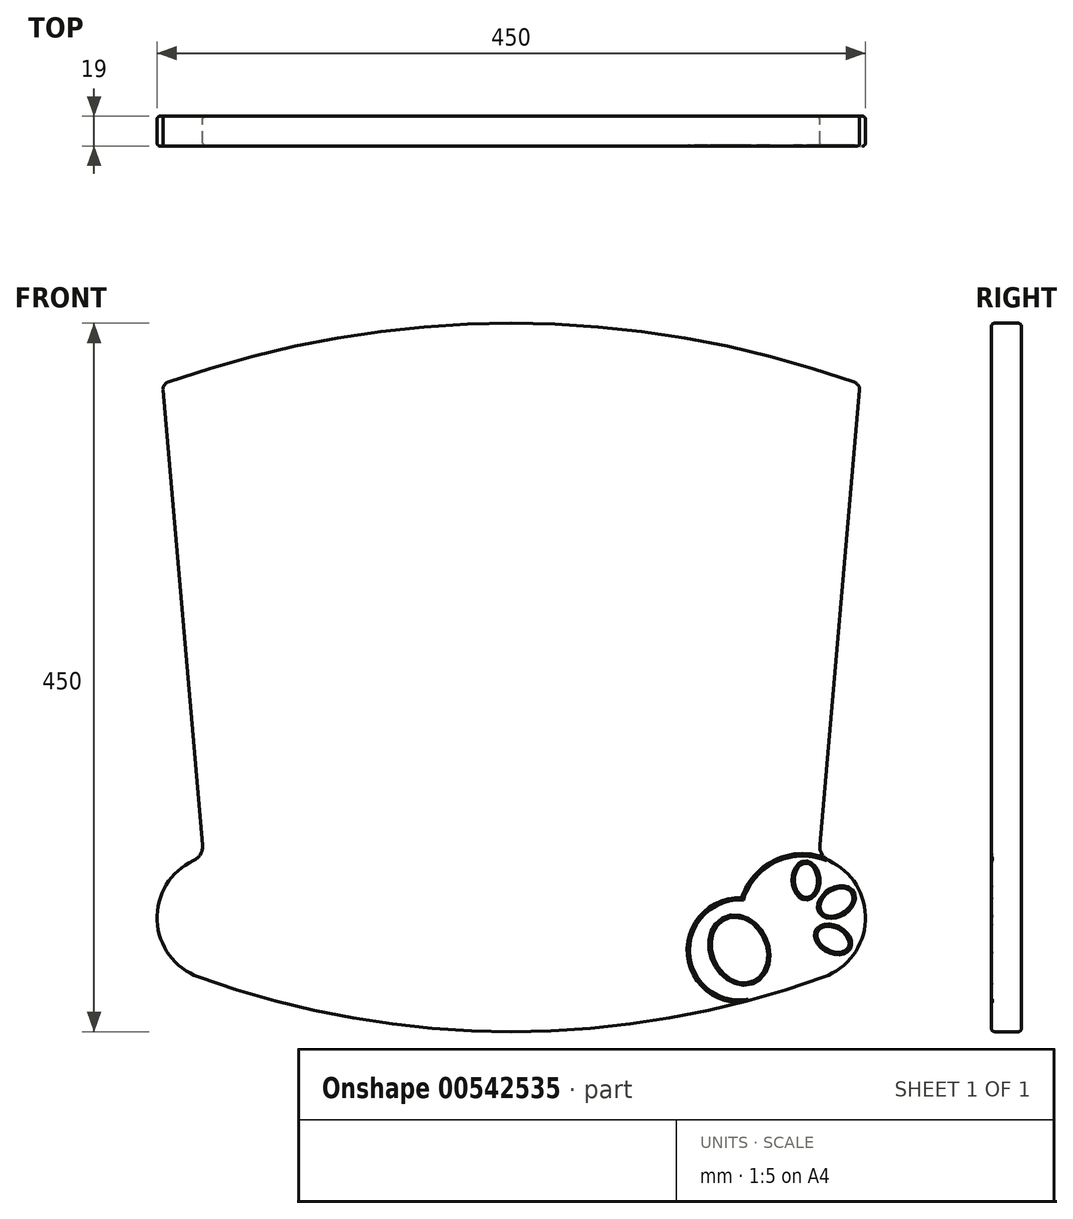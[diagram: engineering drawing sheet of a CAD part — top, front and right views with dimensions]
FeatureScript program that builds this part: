
annotation { "Feature Type Name" : "Feature", "Feature Type Description" : "" }
export const myFeature = defineFeature(function(context is Context, id is Id, definition is map)
    precondition{}
    {
        {
            var Q0;
            Q0=qCreatedBy(makeId("Front.planeOp"),FACE);
            var sketch = newSketch(context, id + "F0", { "sketchPlane" : qUnion([Q0])});
            skLineSegment(sketch, "E0.bottom", {"start": v(225, 450) * mm, "end": v(-225, 450) * mm, "construction": true});
            skLineSegment(sketch, "E0.top", {"start": v(225, 0) * mm, "end": v(-225, 0) * mm, "construction": true});
            skLineSegment(sketch, "E0.left", {"start": v(225, 450) * mm, "end": v(225, 0) * mm, "construction": true});
            skLineSegment(sketch, "E0.right", {"start": v(-225, 450) * mm, "end": v(-225, 0) * mm, "construction": true});
            skArc(sketch, "E1", {"start": v(-198.58, 34.73) * mm, "mid": v(-100.8, 8.75) * mm, "end": v(0, 0) * mm});
            skLineSegment(sketch, "E2", {"start": v(0, 449.93) * mm, "end": v(0, 0) * mm, "construction": true});
            skArc(sketch, "E3", {"start": v(-201.78, 108.67) * mm, "mid": v(-224.96, 70.63) * mm, "end": v(-198.58, 34.73) * mm});
            skPoint(sketch, "E4.orphan", {"position": v(-225, 45) * mm});
            skLineSegment(sketch, "E5", {"start": v(-221.27, 407.4) * mm, "end": v(-196, 118.62) * mm});
            skPoint(sketch, "E6.visualSharp", {"position": v(-195.34, 111) * mm});
            skArc(sketch, "E6.filletArc", {"start": v(-201.78, 108.67) * mm, "mid": v(-197.32, 112.73) * mm, "end": v(-196, 118.62) * mm});
            skArc(sketch, "E7", {"start": v(217.96, 412.54) * mm, "mid": v(0, 450) * mm, "end": v(-217.96, 412.54) * mm});
            skPoint(sketch, "E8.orphan", {"position": v(225, 45) * mm});
            skLineSegment(sketch, "E9.MirrorCS", {"start": v(221.27, 407.4) * mm, "end": v(196, 118.62) * mm});
            skArc(sketch, "E10.MirrorCS", {"start": v(198.58, 34.73) * mm, "mid": v(100.8, 8.75) * mm, "end": v(0, 0) * mm});
            skArc(sketch, "E11.MirrorCS", {"start": v(201.78, 108.67) * mm, "mid": v(224.96, 70.63) * mm, "end": v(198.58, 34.73) * mm});
            skArc(sketch, "E12.MirrorCS", {"start": v(201.78, 108.67) * mm, "mid": v(197.32, 112.73) * mm, "end": v(196, 118.62) * mm});
            skPoint(sketch, "E13.newPointA", {"position": v(-225, 450) * mm});
            skPoint(sketch, "E13.newPointB", {"position": v(-225, 410) * mm});
            skArc(sketch, "E13.filletArc", {"start": v(-217.96, 412.54) * mm, "mid": v(-220.5, 410.53) * mm, "end": v(-221.27, 407.4) * mm});
            skPoint(sketch, "E14.newPointA", {"position": v(225, 410) * mm});
            skPoint(sketch, "E14.newPointB", {"position": v(225, 450) * mm});
            skArc(sketch, "E14.filletArc", {"start": v(221.27, 407.4) * mm, "mid": v(220.5, 410.53) * mm, "end": v(217.96, 412.54) * mm});
            skSolve(sketch);
        }
        {
            var Q0;
            Q0=makeQuery(id+"F0.imprint","IMPRINT",FACE,{"disambiguationData":[TD([[makeQuery(id+"F0.imprint","IMPRINT",EDGE,{"derivedFrom":sQuery(id+"F0.wireOp",EDGE,"E1")}),1.0]])]});
            extrude(context, id + "F1", {"entities" : qUnion([Q0]), "depth" : 19 * mm, "offsetDistance" : 25 * mm});
        }
        {
            var Q0;
            Q0=makeQuery(id+"F1.opExtrude","CAP_FACE",FACE,{"disambiguationData":[OSD([sQuery(id+"F0.wireOp",EDGE,"E1"),sQuery(id+"F0.wireOp",EDGE,"E3"),sQuery(id+"F0.wireOp",EDGE,"E5"),sQuery(id+"F0.wireOp",EDGE,"E6.filletArc"),sQuery(id+"F0.wireOp",EDGE,"E7"),sQuery(id+"F0.wireOp",EDGE,"E9.MirrorCS"),sQuery(id+"F0.wireOp",EDGE,"E10.MirrorCS"),sQuery(id+"F0.wireOp",EDGE,"E11.MirrorCS"),sQuery(id+"F0.wireOp",EDGE,"E12.MirrorCS"),sQuery(id+"F0.wireOp",EDGE,"E13.filletArc"),sQuery(id+"F0.wireOp",EDGE,"E14.filletArc")])],"isStart":false});
            var sketch = newSketch(context, id + "F2", { "sketchPlane" : qUnion([Q0])});
            skArc(sketch, "E15", {"start": v(-153.47, 20.49) * mm, "mid": v(-112.62, 48.48) * mm, "end": v(-146.82, 84.3) * mm});
            skArc(sketch, "E16", {"start": v(146.82, 84.3) * mm, "mid": v(112.62, 48.48) * mm, "end": v(153.47, 20.49) * mm});
            skArc(sketch, "E17", {"start": v(201.78, 108.67) * mm, "mid": v(168.78, 108.92) * mm, "end": v(146.82, 84.3) * mm});
            skArc(sketch, "E18", {"start": v(-146.82, 84.3) * mm, "mid": v(-168.78, 108.92) * mm, "end": v(-201.78, 108.67) * mm});
            skEllipse(sketch, "E19", {"center": v(-187.19, 96) * mm, "majorRadius": 11.57 * mm, "minorRadius": 8.01 * mm, "majorAxis": v(-0.04, -1)});
            skEllipse(sketch, "E20.1.0", {"center": v(-206.57, 82.29) * mm, "majorRadius": 11.57 * mm, "minorRadius": 8.01 * mm, "majorAxis": v(0.84, -0.53)});
            skEllipse(sketch, "E20.2.0", {"center": v(-204.38, 58.65) * mm, "majorRadius": 11.57 * mm, "minorRadius": 8.01 * mm, "majorAxis": v(0.89, 0.46)});
            skLineSegment(sketch, "E20.anchor1", {"start": v(-185, 72.36) * mm, "end": v(-187.19, 96) * mm, "construction": true});
            skLineSegment(sketch, "E20.anchor2", {"start": v(-185, 72.36) * mm, "end": v(-204.38, 58.65) * mm, "construction": true});
            skLineSegment(sketch, "E21", {"start": v(0, 0) * mm, "end": v(0, 96.92) * mm, "construction": true});
            skLineSegment(sketch, "E22", {"start": v(0, 96.92) * mm, "end": v(0, 74.03) * mm});
            skEllipse(sketch, "E23", {"center": v(-144.94, 51.85) * mm, "majorRadius": 17.47 * mm, "minorRadius": 21.85 * mm, "majorAxis": v(-0.92, 0.4)});
            skEllipse(sketch, "E24.MirrorC", {"center": v(144.94, 51.85) * mm, "majorRadius": 17.47 * mm, "minorRadius": 21.85 * mm, "majorAxis": v(0.92, 0.4)});
            skEllipse(sketch, "E25.MirrorC", {"center": v(204.38, 58.65) * mm, "majorRadius": 11.57 * mm, "minorRadius": 8.01 * mm, "majorAxis": v(-0.89, 0.46)});
            skEllipse(sketch, "E26.MirrorC", {"center": v(206.57, 82.29) * mm, "majorRadius": 11.57 * mm, "minorRadius": 8.01 * mm, "majorAxis": v(-0.84, -0.53)});
            skEllipse(sketch, "E27.MirrorC", {"center": v(187.19, 96) * mm, "majorRadius": 11.57 * mm, "minorRadius": 8.01 * mm, "majorAxis": v(0.04, -1)});
            skSolve(sketch);
        }
        {
            var Q0;
            Q0=makeQuery(id+"F1.opExtrude","CAP_VERTEX",VERTEX,{"disambiguationData":[OSD([sQuery(id+"F0.wireOp",EDGE,"E11.MirrorCS"),sQuery(id+"F0.wireOp",EDGE,"E12.MirrorCS")])],"isStart":true});
            var Q1;
            Q1=sQuery(id+"F2.wireOp",VERTEX,"E17.start");
            var Q2;
            Q2=sQuery(id+"F2.wireOp",VERTEX,"E17.center");
            cPlane(context, id + "F3", {"entities" : qUnion([Q0, Q1, Q2]), "cplaneType" : CPlaneType.THREE_POINT, "offset" : 25 * mm, "width" : 150 * mm, "height" : 150 * mm});
        }
        {
            var Q0;
            Q0=qCreatedBy(id+"F3.planeOp",FACE);
            var sketch = newSketch(context, id + "F4", { "sketchPlane" : qUnion([Q0])});
            skPoint(sketch, "E28.0", {"position": v(19, 183.28) * mm});
            skCircle(sketch, "E29", {"center": v(19, 183.28) * mm, "radius": 0.75 * mm});
            skSolve(sketch);
        }
        {
            var Q0;
            Q0=makeQuery(id+"F4.imprint","IMPRINT",FACE,{"disambiguationData":[TD([[makeQuery(id+"F4.imprint","IMPRINT",EDGE,{"derivedFrom":sQuery(id+"F4.wireOp",EDGE,"E29")}),1.0]])]});
            var Q1;
            Q1=sQuery(id+"F2.wireOp",EDGE,"E17");
            var Q2;
            Q2=sQuery(id+"F2.wireOp",EDGE,"E16");
            sweep(context, id + "F5", {"operationType" : NewBodyOperationType.REMOVE, "profiles" : qUnion([Q0]), "path" : qUnion([Q1, Q2])});
        }
        {
            var Q0;
            Q0=makeQuery(id+"F1.opExtrude","CAP_VERTEX",VERTEX,{"disambiguationData":[OSD([sQuery(id+"F0.wireOp",EDGE,"E10.MirrorCS"),sQuery(id+"F0.wireOp",EDGE,"E11.MirrorCS")])],"isStart":true});
            var Q1;
            Q1=makeQuery(id+"F1.opExtrude","CAP_VERTEX",VERTEX,{"disambiguationData":[OSD([sQuery(id+"F0.wireOp",EDGE,"E10.MirrorCS"),sQuery(id+"F0.wireOp",EDGE,"E11.MirrorCS")])],"isStart":false});
            var Q2;
            Q2=sQuery(id+"F2.wireOp",VERTEX,"E16.center");
            cPlane(context, id + "F6", {"entities" : qUnion([Q0, Q1, Q2]), "cplaneType" : CPlaneType.THREE_POINT, "offset" : 25 * mm, "width" : 150 * mm, "height" : 150 * mm});
        }
        {
            var Q0;
            Q0=qCreatedBy(id+"F6.planeOp",FACE);
            var sketch = newSketch(context, id + "F7", { "sketchPlane" : qUnion([Q0])});
            skLineSegment(sketch, "E30.0", {"start": v(141.83, -19) * mm, "end": v(102.8, -19) * mm});
            skCircle(sketch, "E31", {"center": v(102.8, -19) * mm, "radius": 0.75 * mm});
            skSolve(sketch);
        }
        {
            var Q0;
            Q0=makeQuery(id+"F7.imprint","IMPRINT",FACE,{"disambiguationData":[TD([[makeQuery(id+"F7.imprint","IMPRINT",EDGE,{"derivedFrom":sQuery(id+"F7.wireOp",EDGE,"E31")}),1.0]])]});
            var Q1;
            Q1=sQuery(id+"F2.wireOp",EDGE,"E24.MirrorC");
            sweep(context, id + "F8", {"operationType" : NewBodyOperationType.REMOVE, "profiles" : qUnion([Q0]), "path" : qUnion([Q1])});
        }
        {
            var Q0;
            Q0=makeQuery(id+"F1.opExtrude","CAP_VERTEX",VERTEX,{"disambiguationData":[OSD([sQuery(id+"F0.wireOp",EDGE,"E10.MirrorCS"),sQuery(id+"F0.wireOp",EDGE,"E11.MirrorCS")])],"isStart":true});
            var Q1;
            Q1=makeQuery(id+"F1.opExtrude","CAP_VERTEX",VERTEX,{"disambiguationData":[OSD([sQuery(id+"F0.wireOp",EDGE,"E10.MirrorCS"),sQuery(id+"F0.wireOp",EDGE,"E11.MirrorCS")])],"isStart":false});
            var Q2;
            Q2=sQuery(id+"F2.wireOp",VERTEX,"E25.MirrorC.center");
            cPlane(context, id + "F9", {"entities" : qUnion([Q0, Q1, Q2]), "cplaneType" : CPlaneType.THREE_POINT, "offset" : 25 * mm, "width" : 150 * mm, "height" : 150 * mm});
        }
        {
            var Q0;
            Q0=qCreatedBy(id+"F9.planeOp",FACE);
            var sketch = newSketch(context, id + "F10", { "sketchPlane" : qUnion([Q0])});
            skLineSegment(sketch, "E32.0", {"start": v(-19, 96.93) * mm, "end": v(-19, 113.46) * mm});
            skCircle(sketch, "E33", {"center": v(-19, 96.93) * mm, "radius": 0.75 * mm});
            skSolve(sketch);
        }
        {
            var Q0;
            Q0=makeQuery(id+"F10.imprint","IMPRINT",FACE,{"disambiguationData":[TD([[makeQuery(id+"F10.imprint","IMPRINT",EDGE,{"derivedFrom":sQuery(id+"F10.wireOp",EDGE,"E33")}),1.0]])]});
            var Q1;
            Q1=sQuery(id+"F2.wireOp",EDGE,"E25.MirrorC");
            sweep(context, id + "F11", {"operationType" : NewBodyOperationType.REMOVE, "profiles" : qUnion([Q0]), "path" : qUnion([Q1])});
        }
        {
            var Q0;
            Q0=makeQuery(id+"F1.opExtrude","CAP_VERTEX",VERTEX,{"disambiguationData":[OSD([sQuery(id+"F0.wireOp",EDGE,"E10.MirrorCS"),sQuery(id+"F0.wireOp",EDGE,"E11.MirrorCS")])],"isStart":true});
            var Q1;
            Q1=makeQuery(id+"F1.opExtrude","CAP_VERTEX",VERTEX,{"disambiguationData":[OSD([sQuery(id+"F0.wireOp",EDGE,"E10.MirrorCS"),sQuery(id+"F0.wireOp",EDGE,"E11.MirrorCS")])],"isStart":false});
            var Q2;
            Q2=sQuery(id+"F2.wireOp",VERTEX,"E26.MirrorC.center");
            cPlane(context, id + "F12", {"entities" : qUnion([Q0, Q1, Q2]), "cplaneType" : CPlaneType.THREE_POINT, "offset" : 25 * mm, "width" : 150 * mm, "height" : 150 * mm});
        }
        {
            var Q0;
            Q0=qCreatedBy(id+"F12.planeOp",FACE);
            var sketch = newSketch(context, id + "F13", { "sketchPlane" : qUnion([Q0])});
            skLineSegment(sketch, "E34.0", {"start": v(-19, 125.14) * mm, "end": v(-19, 105.62) * mm});
            skCircle(sketch, "E35", {"center": v(-19, 125.14) * mm, "radius": 0.75 * mm});
            skSolve(sketch);
        }
        {
            var Q0;
            Q0=makeQuery(id+"F13.imprint","IMPRINT",FACE,{"disambiguationData":[TD([[makeQuery(id+"F13.imprint","IMPRINT",EDGE,{"derivedFrom":sQuery(id+"F13.wireOp",EDGE,"E35")}),1.0]])]});
            var Q1;
            Q1=sQuery(id+"F2.wireOp",EDGE,"E26.MirrorC");
            sweep(context, id + "F14", {"operationType" : NewBodyOperationType.REMOVE, "profiles" : qUnion([Q0]), "path" : qUnion([Q1])});
        }
        {
            var Q0;
            Q0=makeQuery(id+"F1.opExtrude","CAP_VERTEX",VERTEX,{"disambiguationData":[OSD([sQuery(id+"F0.wireOp",EDGE,"E10.MirrorCS"),sQuery(id+"F0.wireOp",EDGE,"E11.MirrorCS")])],"isStart":true});
            var Q1;
            Q1=makeQuery(id+"F1.opExtrude","CAP_VERTEX",VERTEX,{"disambiguationData":[OSD([sQuery(id+"F0.wireOp",EDGE,"E10.MirrorCS"),sQuery(id+"F0.wireOp",EDGE,"E11.MirrorCS")])],"isStart":false});
            var Q2;
            Q2=sQuery(id+"F2.wireOp",VERTEX,"E27.MirrorC.center");
            cPlane(context, id + "F15", {"entities" : qUnion([Q0, Q1, Q2]), "cplaneType" : CPlaneType.THREE_POINT, "offset" : 25 * mm, "width" : 150 * mm, "height" : 150 * mm});
        }
        {
            var Q0;
            Q0=qCreatedBy(id+"F15.planeOp",FACE);
            var sketch = newSketch(context, id + "F16", { "sketchPlane" : qUnion([Q0])});
            skLineSegment(sketch, "E36.0.0", {"start": v(-19, 71.67) * mm, "end": v(-19, 48.66) * mm});
            skCircle(sketch, "E37", {"center": v(-19, 71.67) * mm, "radius": 0.75 * mm});
            skSolve(sketch);
        }
        {
            var Q0;
            Q0=makeQuery(id+"F16.imprint","IMPRINT",FACE,{"disambiguationData":[TD([[makeQuery(id+"F16.imprint","IMPRINT",EDGE,{"derivedFrom":sQuery(id+"F16.wireOp",EDGE,"E37")}),1.0]])]});
            var Q1;
            Q1=sQuery(id+"F2.wireOp",EDGE,"E27.MirrorC");
            sweep(context, id + "F17", {"operationType" : NewBodyOperationType.REMOVE, "profiles" : qUnion([Q0]), "path" : qUnion([Q1])});
        }
        {
            var Q0;
            Q0=makeQuery(id+"F1.opExtrude","CAP_EDGE",EDGE,{"disambiguationData":[OSD([sQuery(id+"F0.wireOp",EDGE,"E9.MirrorCS")])],"isStart":true});
            fillet(context, id + "F18", {"entities" : qUnion([Q0]), "radius" : 2 * mm, "tangentPropagation" : true, "allowEdgeOverflow" : false});
        }
        {
            var Q0;
            Q0=makeQuery(id+"F1.opExtrude","CAP_EDGE",EDGE,{"disambiguationData":[OSD([sQuery(id+"F0.wireOp",EDGE,"E5")])],"isStart":false});
            var Q1;
            {var subQ0=sQuery(id+"F0.wireOp",EDGE,"E10.MirrorCS");var subQ1=sQuery(id+"F0.wireOp",EDGE,"E3");var subQ2=sQuery(id+"F0.wireOp",EDGE,"E1");var subQ5=sQuery(id+"F4.wireOp",EDGE,"E29");var subQ6=sQuery(id+"F2.wireOp",EDGE,"E16");var subQ7=makeQuery(id+"F5.opSweep","SWEPT_FACE",FACE,{"disambiguationData":[OSD([subQ6,subQ5])]});Q1=makeQuery(id+"FvVFnBOKG56wCRS_1.1.F5.boolean.opBoolean","SPLIT",EDGE,{"disambiguationData":[TD([makeQuery(id+"F5.boolean.opBoolean","COPY",FACE,{"derivedFrom":subQ7})])],"derivedFrom":makeQuery(id+"F5.boolean.opBoolean","SPLIT",EDGE,{"disambiguationData":[TD([makeQuery(id+"F1.opExtrude","SWEPT_FACE",FACE,{"disambiguationData":[OSD([subQ1])]})])],"derivedFrom":makeQuery(id+"F1.opExtrude","CAP_EDGE",EDGE,{"disambiguationData":[OSD([subQ2,subQ0])],"isStart":false})})});}
            fillet(context, id + "F19", {"entities" : qUnion([Q0, Q1]), "radius" : 2 * mm, "tangentPropagation" : true, "allowEdgeOverflow" : false});
        }
        {
            var Q0;
            Q0=makeQuery(id+"F1.opExtrude","CAP_EDGE",EDGE,{"disambiguationData":[OSD([sQuery(id+"F0.wireOp",EDGE,"E11.MirrorCS")])],"isStart":false});
            var Q1;
            Q1=makeQuery(id+"F1.opExtrude","CAP_EDGE",EDGE,{"disambiguationData":[OSD([sQuery(id+"F0.wireOp",EDGE,"E3")])],"isStart":false});
            fillet(context, id + "F20", {"entities" : qUnion([Q0, Q1]), "radius" : 2 * mm, "tangentPropagation" : true, "allowEdgeOverflow" : false});
        }
    });
